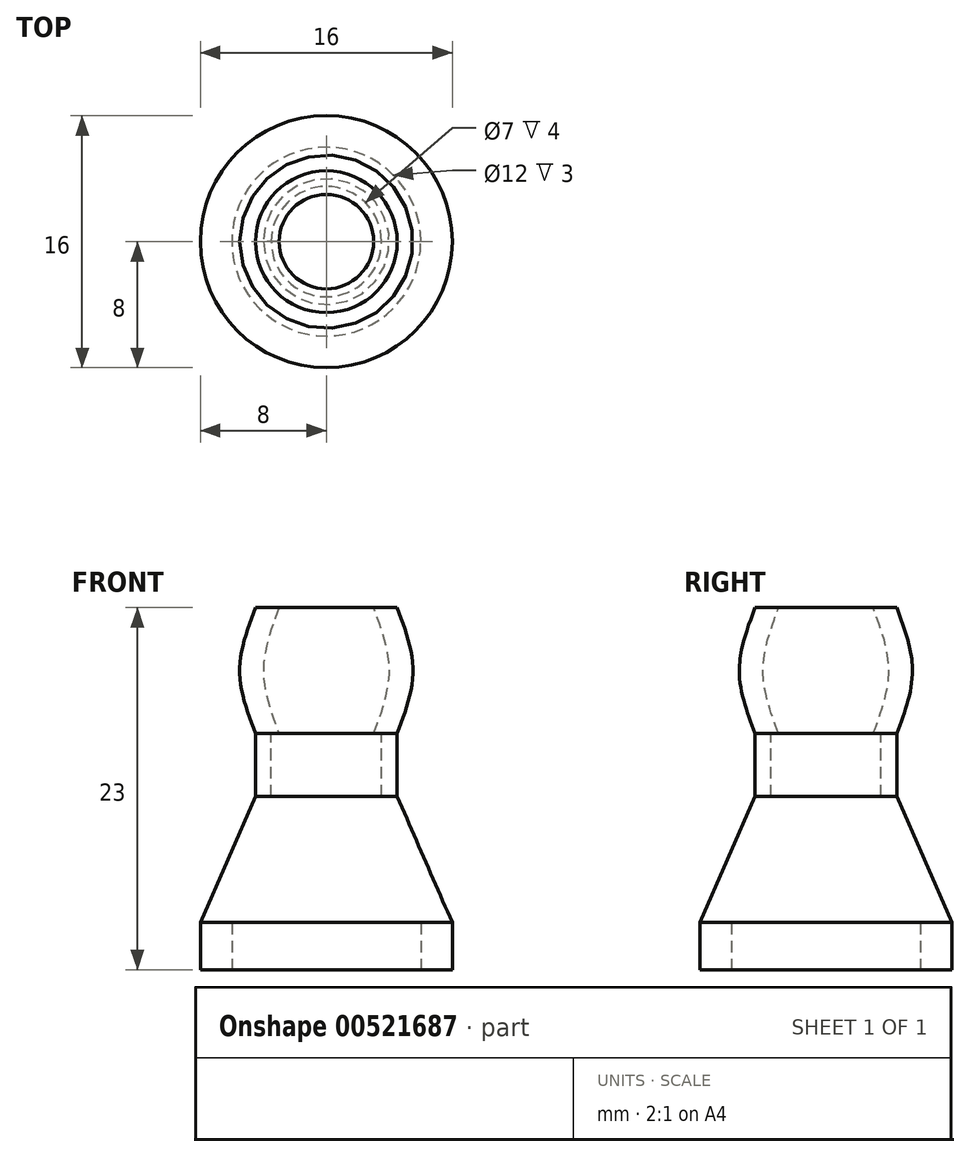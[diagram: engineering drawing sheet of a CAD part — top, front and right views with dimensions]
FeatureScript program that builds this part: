
annotation { "Feature Type Name" : "Feature", "Feature Type Description" : "" }
export const myFeature = defineFeature(function(context is Context, id is Id, definition is map)
    precondition{}
    {
        {
            var Q0;
            Q0=qCreatedBy(makeId("Top.planeOp"),FACE);
            var sketch = newSketch(context, id + "F0", { "sketchPlane" : qUnion([Q0])});
            skCircle(sketch, "E0", {"center": v(0, 0) * mm, "radius": 6 * mm});
            skCircle(sketch, "E1", {"center": v(0, 0) * mm, "radius": 8 * mm});
            skSolve(sketch);
        }
        {
            var Q0;
            Q0=makeQuery(id+"F0.imprint","IMPRINT",FACE,{"disambiguationData":[TD([[makeQuery(id+"F0.imprint","IMPRINT",EDGE,{"derivedFrom":sQuery(id+"F0.wireOp",EDGE,"E0")}),-1.0]])]});
            cPlane(context, id + "F1", {"entities" : qUnion([Q0]), "cplaneType" : CPlaneType.OFFSET, "offset" : 3 * mm, "width" : 150 * mm, "height" : 150 * mm});
        }
        {
            var Q0;
            Q0=qCreatedBy(id+"F1.planeOp",FACE);
            var sketch = newSketch(context, id + "F2", { "sketchPlane" : qUnion([Q0])});
            skCircle(sketch, "E2.0", {"center": v(0, 0) * mm, "radius": 6 * mm, "construction": true});
            skCircle(sketch, "E3.0", {"center": v(0, 0) * mm, "radius": 8 * mm});
            skSolve(sketch);
        }
        {
            var Q0;
            Q0=qCreatedBy(id+"F1.planeOp",FACE);
            cPlane(context, id + "F3", {"entities" : qUnion([Q0]), "cplaneType" : CPlaneType.OFFSET, "offset" : 8 * mm, "width" : 150 * mm, "height" : 150 * mm});
        }
        {
            var Q0;
            Q0=qCreatedBy(id+"F3.planeOp",FACE);
            var sketch = newSketch(context, id + "F4", { "sketchPlane" : qUnion([Q0])});
            skPoint(sketch, "E4.0", {"position": v(0, 0) * mm});
            skCircle(sketch, "E5", {"center": v(0, 0) * mm, "radius": 4.5 * mm});
            skCircle(sketch, "E6", {"center": v(0, 0) * mm, "radius": 3.5 * mm, "construction": true});
            skSolve(sketch);
        }
        {
            var Q0;
            Q0=qCreatedBy(id+"F3.planeOp",FACE);
            cPlane(context, id + "F5", {"entities" : qUnion([Q0]), "cplaneType" : CPlaneType.OFFSET, "offset" : 4 * mm, "width" : 150 * mm, "height" : 150 * mm});
        }
        {
            var Q0;
            Q0=qCreatedBy(id+"F5.planeOp",FACE);
            var sketch = newSketch(context, id + "F6", { "sketchPlane" : qUnion([Q0])});
            skCircle(sketch, "E7.0", {"center": v(0, 0) * mm, "radius": 4.5 * mm});
            skCircle(sketch, "E8.0", {"center": v(0, 0) * mm, "radius": 3.5 * mm});
            skSolve(sketch);
        }
        {
            var Q0;
            Q0=qCreatedBy(makeId("Front.planeOp"),FACE);
            var sketch = newSketch(context, id + "F7", { "sketchPlane" : qUnion([Q0])});
            skPoint(sketch, "E9.0", {"position": v(0, 15) * mm});
            skLineSegment(sketch, "E10", {"start": v(0, 15) * mm, "end": v(0, 23) * mm, "construction": true});
            skLineSegment(sketch, "E11", {"start": v(0, 19) * mm, "end": v(5.5, 19) * mm, "construction": true});
            skLineSegment(sketch, "E12", {"start": v(0, 23) * mm, "end": v(3, 23) * mm, "construction": true});
            skLineSegment(sketch, "E13", {"start": v(0, 15) * mm, "end": v(3, 15) * mm, "construction": true});
            skLineSegment(sketch, "E14", {"start": v(0, 23) * mm, "end": v(4.5, 23) * mm});
            skLineSegment(sketch, "E15", {"start": v(0, 15) * mm, "end": v(4.5, 15) * mm});
            skPoint(sketch, "E16", {"position": v(4, 19) * mm});
            skFitSpline(sketch, "E17", {"points": [v(3, 23) * mm, v(4, 19) * mm, v(3, 15) * mm], "startDerivative": vector(3, -8) * mm, "endDerivative": vector(-3, -8) * mm});
            skFitSpline(sketch, "E18", {"points": [v(4.5, 23) * mm, v(5.5, 19) * mm, v(4.5, 15) * mm], "startDerivative": vector(3, -8) * mm, "endDerivative": vector(-3, -8) * mm});
            skSolve(sketch);
        }
        {
            var Q0;
            {var subQ2=sQuery(id+"F7.wireOp",EDGE,"E17");Q0=makeQuery(id+"F7.imprint","IMPRINT",FACE,{"disambiguationData":[TD([[makeQuery(id+"F7.imprint","IMPRINT",EDGE,{"derivedFrom":subQ2}),1.0]])]});}
            var Q1;
            Q1=sQuery(id+"F7.wireOp",EDGE,"E10");
            revolve(context, id + "F8", {"entities" : qUnion([Q0]), "axis" : qUnion([Q1]), "revolveType" : RevolveType.FULL});
        }
        {
            var Q0;
            Q0=makeQuery(id+"F6.imprint","IMPRINT",FACE,{"disambiguationData":[TD([[makeQuery(id+"F6.imprint","IMPRINT",EDGE,{"derivedFrom":sQuery(id+"F6.wireOp",EDGE,"E7.0")}),1.0]])]});
            var Q1;
            Q1=qCreatedBy(id+"F3.planeOp",FACE);
            extrude(context, id + "F9", {"entities" : qUnion([Q0]), "operationType" : NewBodyOperationType.ADD, "endBound" : BoundingType.UP_TO_SURFACE, "oppositeDirection" : true, "depth" : 25 * mm, "endBoundEntityFace" : qUnion([Q1]), "offsetDistance" : 25 * mm});
        }
        {
            var Q0;
            Q0=makeQuery(id+"F0.imprint","IMPRINT",FACE,{"disambiguationData":[TD([[makeQuery(id+"F0.imprint","IMPRINT",EDGE,{"derivedFrom":sQuery(id+"F0.wireOp",EDGE,"E0")}),-1.0]])]});
            var Q1;
            Q1=qCreatedBy(id+"F1.planeOp",FACE);
            extrude(context, id + "F10", {"entities" : qUnion([Q0]), "endBound" : BoundingType.UP_TO_SURFACE, "depth" : 25 * mm, "endBoundEntityFace" : qUnion([Q1]), "offsetDistance" : 25 * mm});
        }
        {
            var Q0;
            Q0=makeQuery(id+"F2.imprint","IMPRINT",FACE,{"disambiguationData":[TD([[makeQuery(id+"F2.imprint","IMPRINT",EDGE,{"derivedFrom":sQuery(id+"F2.wireOp",EDGE,"E3.0")}),1.0]])]});
            var Q1;
            Q1=makeQuery(id+"F4.imprint","IMPRINT",FACE,{"disambiguationData":[TD([[makeQuery(id+"F4.imprint","IMPRINT",EDGE,{"derivedFrom":sQuery(id+"F4.wireOp",EDGE,"E5")}),1.0]])]});
            loft(context, id + "F11", {"operationType" : NewBodyOperationType.ADD, "sheetProfilesArray" : [{ "sheetProfileEntities" : qUnion([Q0]) }, { "sheetProfileEntities" : qUnion([Q1]) }]});
        }
    });
